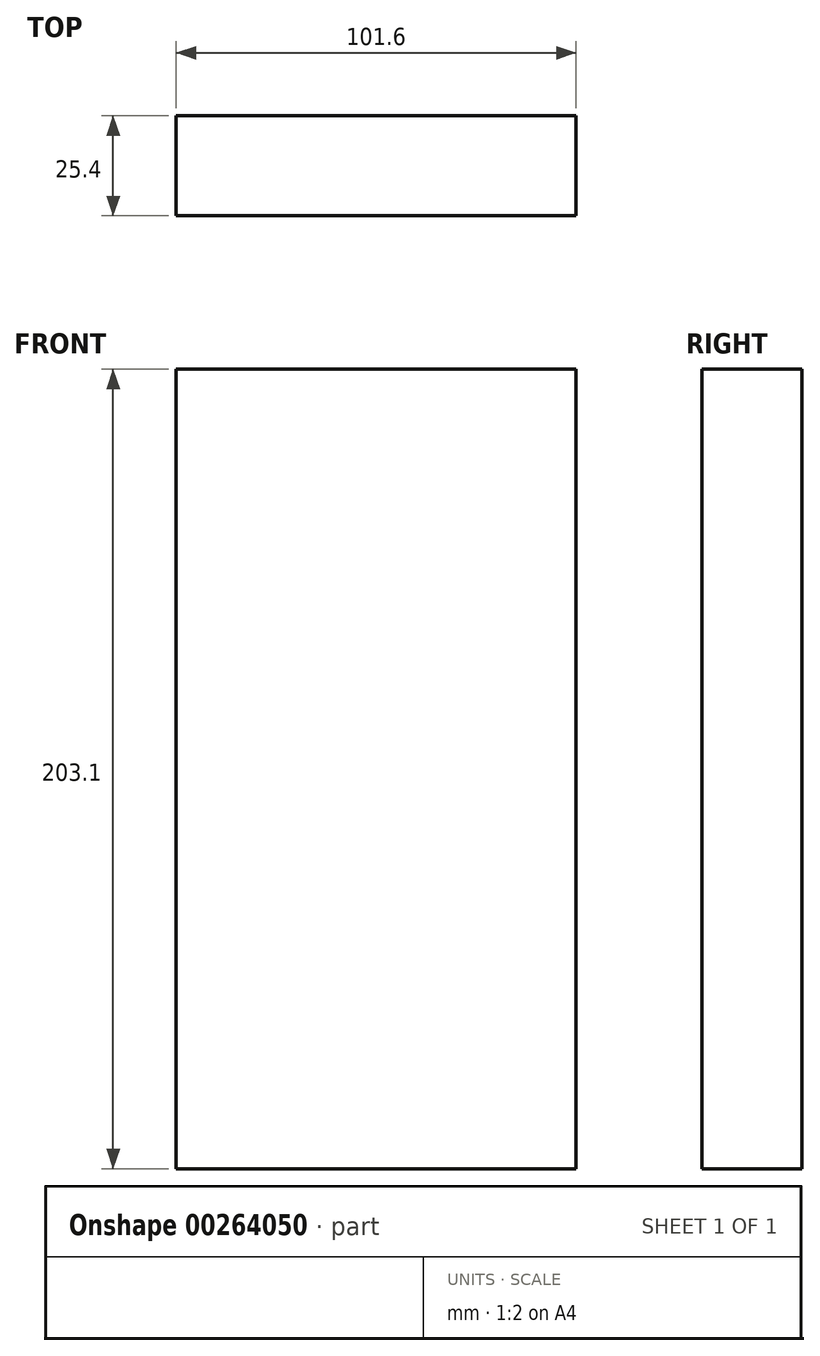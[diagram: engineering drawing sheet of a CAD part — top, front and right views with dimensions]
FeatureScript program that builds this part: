
annotation { "Feature Type Name" : "Feature", "Feature Type Description" : "" }
export const myFeature = defineFeature(function(context is Context, id is Id, definition is map)
    precondition{}
    {
        {
            var Q0;
            Q0=qCreatedBy(makeId("Front.planeOp"),FACE);
            var sketch = newSketch(context, id + "F0", { "sketchPlane" : qUnion([Q0])});
            skLineSegment(sketch, "E0.bottom", {"start": v(-21.37, -45.4) * mm, "end": v(80.23, -45.4) * mm});
            skLineSegment(sketch, "E0.top", {"start": v(-21.37, 157.7) * mm, "end": v(80.23, 157.7) * mm});
            skLineSegment(sketch, "E0.left", {"start": v(-21.37, -45.4) * mm, "end": v(-21.37, 157.7) * mm});
            skLineSegment(sketch, "E0.right", {"start": v(80.23, -45.4) * mm, "end": v(80.23, 157.7) * mm});
            skSolve(sketch);
        }
        {
            var Q0;
            Q0=makeQuery(id+"F0.imprint","IMPRINT",FACE,{"disambiguationData":[TD([[makeQuery(id+"F0.imprint","IMPRINT",EDGE,{"derivedFrom":sQuery(id+"F0.wireOp",EDGE,"E0.bottom")}),1.0]])]});
            extrude(context, id + "F1", {"entities" : qUnion([Q0]), "oppositeDirection" : true, "depth" : 25.4 * mm});
        }
    });
